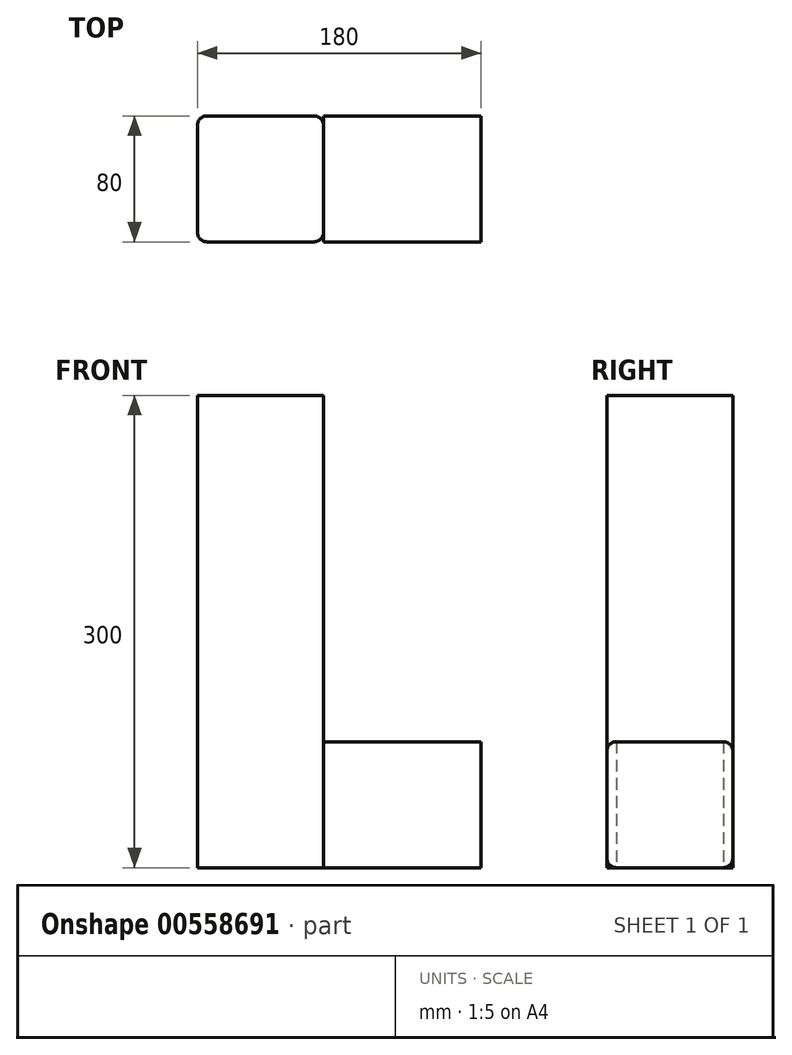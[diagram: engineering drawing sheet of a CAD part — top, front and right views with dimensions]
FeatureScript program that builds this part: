
annotation { "Feature Type Name" : "Feature", "Feature Type Description" : "" }
export const myFeature = defineFeature(function(context is Context, id is Id, definition is map)
    precondition{}
    {
        {
            var Q0;
            Q0=qCreatedBy(makeId("Top.planeOp"),FACE);
            var sketch = newSketch(context, id + "F0", { "sketchPlane" : qUnion([Q0])});
            skLineSegment(sketch, "E0.bottom", {"start": v(0, 0) * mm, "end": v(-80, 0) * mm});
            skLineSegment(sketch, "E0.top", {"start": v(0, 80) * mm, "end": v(-80, 80) * mm});
            skLineSegment(sketch, "E0.left", {"start": v(0, 0) * mm, "end": v(0, 80) * mm});
            skLineSegment(sketch, "E0.right", {"start": v(-80, 0) * mm, "end": v(-80, 80) * mm});
            skSolve(sketch);
        }
        {
            var Q0;
            Q0 = qSketchRegion(id + "F0", true);
            extrude(context, id + "F1", {"entities" : qUnion([Q0]), "depth" : 300 * mm, "offsetDistance" : 25.4 * mm});
        }
        {
            var Q0;
            Q0=makeQuery(id+"F1.opExtrude","SWEPT_EDGE",EDGE,{"disambiguationData":[OSD([sQuery(id+"F0.wireOp",EDGE,"E0.top"),sQuery(id+"F0.wireOp",EDGE,"E0.right")])]});
            var Q1;
            Q1=makeQuery(id+"F1.opExtrude","SWEPT_EDGE",EDGE,{"disambiguationData":[OSD([sQuery(id+"F0.wireOp",EDGE,"E0.bottom"),sQuery(id+"F0.wireOp",EDGE,"E0.right")])]});
            var Q2;
            Q2=makeQuery(id+"F1.opExtrude","SWEPT_EDGE",EDGE,{"disambiguationData":[OSD([sQuery(id+"F0.wireOp",EDGE,"E0.bottom"),sQuery(id+"F0.wireOp",EDGE,"E0.left")])]});
            var Q3;
            Q3=makeQuery(id+"F1.opExtrude","SWEPT_EDGE",EDGE,{"disambiguationData":[OSD([sQuery(id+"F0.wireOp",EDGE,"E0.top"),sQuery(id+"F0.wireOp",EDGE,"E0.left")])]});
            fillet(context, id + "F2", {"entities" : qUnion([Q0, Q1, Q2, Q3]), "radius" : 6 * mm, "tangentPropagation" : true, "allowEdgeOverflow" : false});
        }
        {
            var Q0;
            Q0=qCreatedBy(makeId("Right.planeOp"),FACE);
            var sketch = newSketch(context, id + "F3", { "sketchPlane" : qUnion([Q0])});
            skLineSegment(sketch, "E1.bottom", {"start": v(0, 0) * mm, "end": v(80, 0) * mm});
            skLineSegment(sketch, "E1.top", {"start": v(0, 80) * mm, "end": v(80, 80) * mm});
            skLineSegment(sketch, "E1.left", {"start": v(0, 0) * mm, "end": v(0, 80) * mm});
            skLineSegment(sketch, "E1.right", {"start": v(80, 0) * mm, "end": v(80, 80) * mm});
            skSolve(sketch);
        }
        {
            var Q0;
            Q0 = qSketchRegion(id + "F3", true);
            extrude(context, id + "F4", {"entities" : qUnion([Q0]), "operationType" : NewBodyOperationType.ADD, "depth" : 100 * mm, "offsetDistance" : 25.4 * mm});
        }
        {
            var Q0;
            Q0=makeQuery(id+"F4.opExtrude","SWEPT_EDGE",EDGE,{"disambiguationData":[OSD([sQuery(id+"F3.wireOp",EDGE,"E1.top"),sQuery(id+"F3.wireOp",EDGE,"E1.left")])]});
            var Q1;
            Q1=makeQuery(id+"F4.opExtrude","SWEPT_EDGE",EDGE,{"disambiguationData":[OSD([sQuery(id+"F3.wireOp",EDGE,"E1.top"),sQuery(id+"F3.wireOp",EDGE,"E1.right")])]});
            var Q2;
            Q2=makeQuery(id+"F4.opExtrude","SWEPT_EDGE",EDGE,{"disambiguationData":[OSD([sQuery(id+"F3.wireOp",EDGE,"E1.bottom"),sQuery(id+"F3.wireOp",EDGE,"E1.left")])]});
            var Q3;
            Q3=makeQuery(id+"F4.opExtrude","SWEPT_EDGE",EDGE,{"disambiguationData":[OSD([sQuery(id+"F3.wireOp",EDGE,"E1.bottom"),sQuery(id+"F3.wireOp",EDGE,"E1.right")])]});
            fillet(context, id + "F5", {"entities" : qUnion([Q0, Q1, Q2, Q3]), "radius" : 6 * mm, "tangentPropagation" : true, "allowEdgeOverflow" : false});
        }
    });
